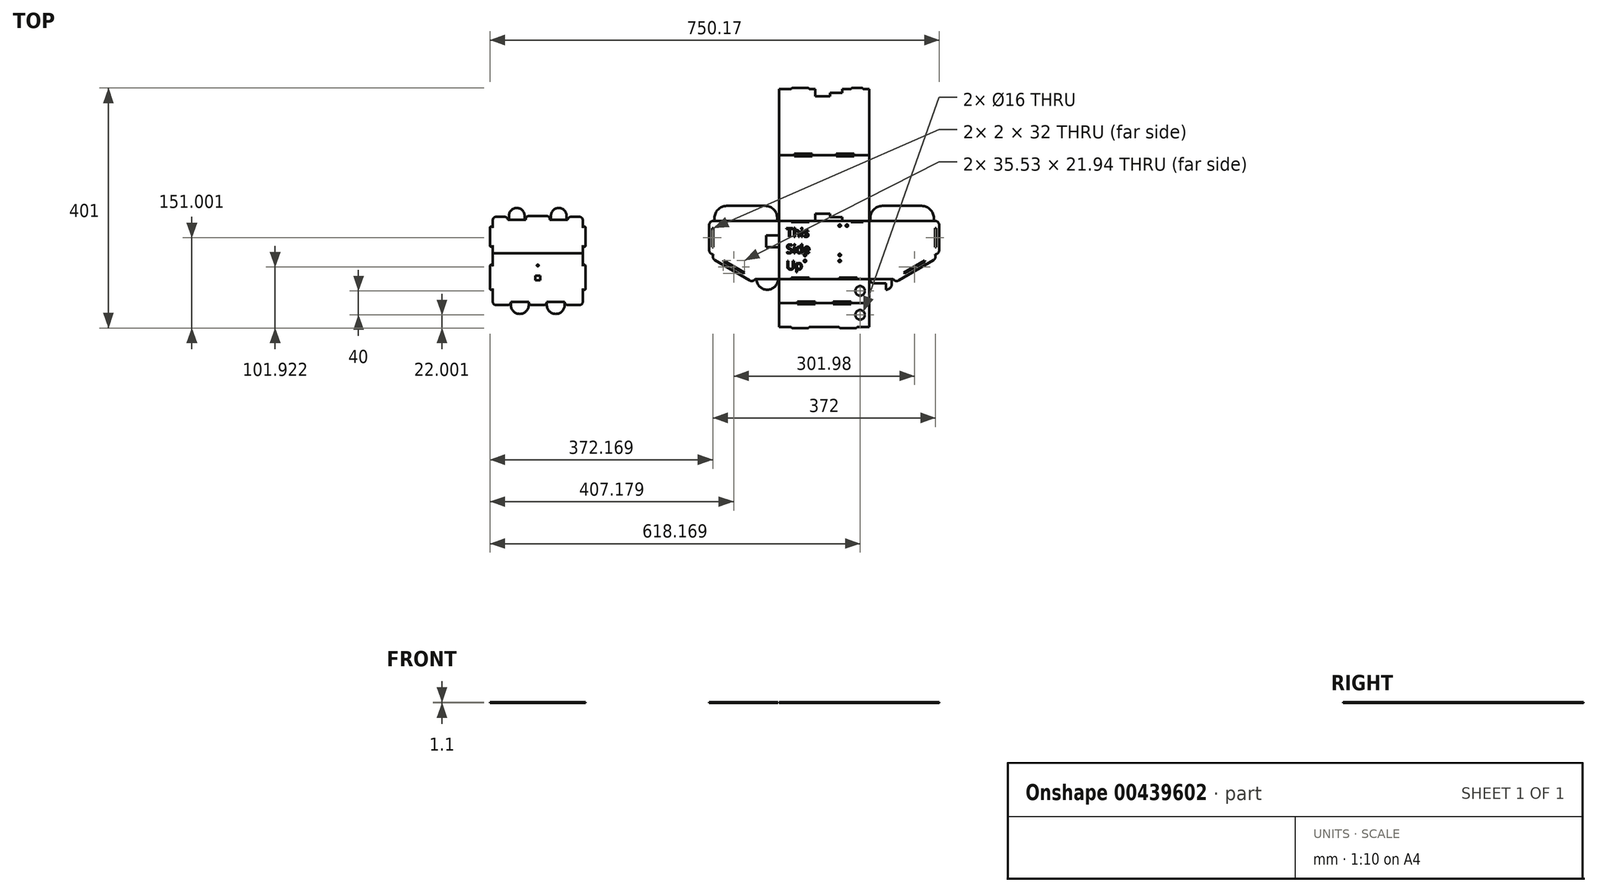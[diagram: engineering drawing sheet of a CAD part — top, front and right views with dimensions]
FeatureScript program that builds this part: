
annotation { "Feature Type Name" : "Feature", "Feature Type Description" : "" }
export const myFeature = defineFeature(function(context is Context, id is Id, definition is map)
    precondition{}
    {
        {
            var Q0;
            Q0=qCreatedBy(makeId("Top.planeOp"),FACE);
            var sketch = newSketch(context, id + "F0", { "sketchPlane" : qUnion([Q0])});
            skLineSegment(sketch, "E0.bottom", {"start": v(-62.15, 54.37) * mm, "end": v(87.85, 54.37) * mm});
            skLineSegment(sketch, "E0.top", {"start": v(-62.15, -42.63) * mm, "end": v(87.85, -42.63) * mm});
            skLineSegment(sketch, "E0.left", {"start": v(-62.15, 54.37) * mm, "end": v(-62.15, -42.63) * mm});
            skLineSegment(sketch, "E0.right", {"start": v(87.85, 54.37) * mm, "end": v(87.85, -42.63) * mm});
            skSolve(sketch);
        }
        {
            var Q0;
            Q0 = qSketchRegion(id + "F0", true);
            extrude(context, id + "F1", {"entities" : qUnion([Q0]), "depth" : 1 * mm});
        }
        {
            var Q0;
            Q0=qCreatedBy(makeId("Top.planeOp"),FACE);
            var sketch = newSketch(context, id + "F2", { "sketchPlane" : qUnion([Q0])});
            skLineSegment(sketch, "E1", {"start": v(-62.15, 54.37) * mm, "end": v(-62.15, -42.63) * mm});
            skLineSegment(sketch, "E2", {"start": v(-172.15, -1.63) * mm, "end": v(-172.15, 54.37) * mm});
            skLineSegment(sketch, "E3", {"start": v(-172.15, 54.37) * mm, "end": v(-62.15, 54.37) * mm});
            skPoint(sketch, "E4", {"position": v(-62.15, 5.87) * mm});
            skLineSegment(sketch, "E5", {"start": v(-62.15, -42.63) * mm, "end": v(-102.15, -42.63) * mm});
            skLineSegment(sketch, "E6", {"start": v(-102.15, -42.63) * mm, "end": v(-172.15, -1.63) * mm});
            skLineSegment(sketch, "E7.bottom", {"start": v(-172.15, 54.37) * mm, "end": v(-172.15, 54.37) * mm});
            skLineSegment(sketch, "E7.top", {"start": v(-172.15, -1.63) * mm, "end": v(-172.15, -1.63) * mm});
            skLineSegment(sketch, "E7.left", {"start": v(-172.15, 54.37) * mm, "end": v(-172.15, -1.63) * mm});
            skLineSegment(sketch, "E7.right", {"start": v(-179.15, 47.37) * mm, "end": v(-179.15, 5.37) * mm});
            skPoint(sketch, "E8.visualSharp", {"position": v(-179.15, 54.37) * mm});
            skArc(sketch, "E8.filletArc", {"start": v(-172.15, 54.37) * mm, "mid": v(-177.1, 52.32) * mm, "end": v(-179.15, 47.37) * mm});
            skPoint(sketch, "E9.visualSharp", {"position": v(-179.15, -1.63) * mm});
            skArc(sketch, "E9.filletArc", {"start": v(-179.15, 5.37) * mm, "mid": v(-177.1, 0.42) * mm, "end": v(-172.15, -1.63) * mm});
            skLineSegment(sketch, "E10", {"start": v(-172.15, -1.63) * mm, "end": v(-102.15, -42.63) * mm});
            skLineSegment(sketch, "E11", {"start": v(-102.15, -42.63) * mm, "end": v(-102.15, -42.63) * mm});
            skLineSegment(sketch, "E12", {"start": v(-111.73, -45.13) * mm, "end": v(-169.65, -11.2) * mm});
            skPoint(sketch, "E13.visualSharp", {"position": v(-175.69, -7.67) * mm});
            skArc(sketch, "E13.filletArc", {"start": v(-172.15, -1.63) * mm, "mid": v(-172.88, -6.94) * mm, "end": v(-169.65, -11.2) * mm});
            skPoint(sketch, "E14.visualSharp", {"position": v(-105.69, -48.67) * mm});
            skArc(sketch, "E14.filletArc", {"start": v(-111.73, -45.13) * mm, "mid": v(-106.42, -45.86) * mm, "end": v(-102.15, -42.63) * mm});
            skSolve(sketch);
        }
        {
            var Q0;
            Q0 = qSketchRegion(id + "F2", true);
            extrude(context, id + "F3", {"entities" : qUnion([Q0]), "depth" : 1 * mm});
        }
        {
            var Q0;
            Q0=makeQuery(id+"F3.opExtrude","CAP_FACE",FACE,{"disambiguationData":[OSD([sQuery(id+"F2.wireOp",EDGE,"E1"),sQuery(id+"F2.wireOp",EDGE,"Gzizx2Oh-LAW5-sl6d-gqP5-EabzbZT4bnnK"),sQuery(id+"F2.wireOp",EDGE,"E2"),sQuery(id+"F2.wireOp",EDGE,"E3")])],"isStart":false});
            var sketch = newSketch(context, id + "F4", { "sketchPlane" : qUnion([Q0])});
            skLineSegment(sketch, "E15.bottom", {"start": v(-62.15, 30.37) * mm, "end": v(-84.15, 30.37) * mm});
            skLineSegment(sketch, "E15.top", {"start": v(-62.15, 10.37) * mm, "end": v(-84.15, 10.37) * mm});
            skLineSegment(sketch, "E15.left", {"start": v(-62.15, 30.37) * mm, "end": v(-62.15, 10.37) * mm});
            skLineSegment(sketch, "E15.right", {"start": v(-84.15, 30.37) * mm, "end": v(-84.15, 10.37) * mm});
            skLineSegment(sketch, "E16", {"start": v(-154.9, -11.74) * mm, "end": v(-120.38, -31.95) * mm});
            skLineSegment(sketch, "E17", {"start": v(-154.9, -11.74) * mm, "end": v(-155.9, -13.46) * mm});
            skLineSegment(sketch, "E18", {"start": v(-155.9, -13.46) * mm, "end": v(-121.39, -33.68) * mm});
            skLineSegment(sketch, "E19", {"start": v(-121.39, -33.68) * mm, "end": v(-120.38, -31.95) * mm});
            skLineSegment(sketch, "E20.bottom", {"start": v(-172.15, 42.37) * mm, "end": v(-174.15, 42.37) * mm});
            skLineSegment(sketch, "E20.top", {"start": v(-172.15, 10.37) * mm, "end": v(-174.15, 10.37) * mm});
            skLineSegment(sketch, "E20.left", {"start": v(-172.15, 42.37) * mm, "end": v(-172.15, 10.37) * mm});
            skLineSegment(sketch, "E20.right", {"start": v(-174.15, 42.37) * mm, "end": v(-174.15, 10.37) * mm});
            skSolve(sketch);
        }
        {
            var Q0;
            Q0 = qSketchRegion(id + "F4", true);
            extrude(context, id + "F5", {"entities" : qUnion([Q0]), "operationType" : NewBodyOperationType.REMOVE, "oppositeDirection" : true, "depth" : 1 * mm});
        }
        {
            var Q0;
            Q0=qCreatedBy(makeId("Top.planeOp"),FACE);
            var sketch = newSketch(context, id + "F6", { "sketchPlane" : qUnion([Q0])});
            skLineSegment(sketch, "E21", {"start": v(87.85, 54.37) * mm, "end": v(197.85, 54.37) * mm});
            skLineSegment(sketch, "E22", {"start": v(197.85, 54.37) * mm, "end": v(197.85, -1.63) * mm});
            skLineSegment(sketch, "E23", {"start": v(87.85, -42.63) * mm, "end": v(87.85, 54.37) * mm});
            skLineSegment(sketch, "E24", {"start": v(87.85, -42.63) * mm, "end": v(127.85, -42.63) * mm});
            skLineSegment(sketch, "E25", {"start": v(127.85, -42.63) * mm, "end": v(197.85, -1.63) * mm});
            skLineSegment(sketch, "E26.bottom", {"start": v(197.85, 54.37) * mm, "end": v(197.85, 54.37) * mm});
            skLineSegment(sketch, "E26.top", {"start": v(197.85, -1.63) * mm, "end": v(197.85, -1.63) * mm});
            skLineSegment(sketch, "E26.right", {"start": v(204.85, 47.37) * mm, "end": v(204.85, 5.37) * mm});
            skLineSegment(sketch, "E27", {"start": v(195.35, -11.2) * mm, "end": v(137.43, -45.13) * mm});
            skLineSegment(sketch, "E28", {"start": v(127.85, -42.63) * mm, "end": v(127.85, -42.63) * mm});
            skPoint(sketch, "E29.visualSharp", {"position": v(131.39, -48.67) * mm});
            skArc(sketch, "E29.filletArc", {"start": v(127.85, -42.63) * mm, "mid": v(132.12, -45.86) * mm, "end": v(137.43, -45.13) * mm});
            skPoint(sketch, "E30.visualSharp", {"position": v(201.39, -7.67) * mm});
            skArc(sketch, "E30.filletArc", {"start": v(195.35, -11.2) * mm, "mid": v(198.58, -6.94) * mm, "end": v(197.85, -1.63) * mm});
            skPoint(sketch, "E31.visualSharp", {"position": v(204.85, -1.63) * mm});
            skArc(sketch, "E31.filletArc", {"start": v(197.85, -1.63) * mm, "mid": v(202.8, 0.42) * mm, "end": v(204.85, 5.37) * mm});
            skPoint(sketch, "E32.visualSharp", {"position": v(204.85, 54.37) * mm});
            skArc(sketch, "E32.filletArc", {"start": v(204.85, 47.37) * mm, "mid": v(202.8, 52.32) * mm, "end": v(197.85, 54.37) * mm});
            skSolve(sketch);
        }
        {
            var Q0;
            Q0 = qSketchRegion(id + "F6", true);
            extrude(context, id + "F7", {"entities" : qUnion([Q0]), "depth" : 1 * mm});
        }
        {
            var Q0;
            Q0=qCreatedBy(makeId("Top.planeOp"),FACE);
            var sketch = newSketch(context, id + "F8", { "sketchPlane" : qUnion([Q0])});
            skLineSegment(sketch, "E33.bottom", {"start": v(-62.15, 54.37) * mm, "end": v(87.85, 54.37) * mm});
            skLineSegment(sketch, "E33.top", {"start": v(-62.15, 164.37) * mm, "end": v(87.85, 164.37) * mm});
            skLineSegment(sketch, "E33.left", {"start": v(-62.15, 54.37) * mm, "end": v(-62.15, 164.37) * mm});
            skLineSegment(sketch, "E33.right", {"start": v(87.85, 54.37) * mm, "end": v(87.85, 164.37) * mm});
            skSolve(sketch);
        }
        {
            var Q0;
            Q0 = qSketchRegion(id + "F8", true);
            extrude(context, id + "F9", {"entities" : qUnion([Q0]), "depth" : 1 * mm});
        }
        {
            var Q0;
            Q0=makeQuery(id+"F9.opExtrude","CAP_FACE",FACE,{"disambiguationData":[OSD([sQuery(id+"F8.wireOp",EDGE,"E33.bottom"),sQuery(id+"F8.wireOp",EDGE,"E33.top"),sQuery(id+"F8.wireOp",EDGE,"E33.left"),sQuery(id+"F8.wireOp",EDGE,"E33.right")])],"isStart":false});
            var sketch = newSketch(context, id + "F10", { "sketchPlane" : qUnion([Q0])});
            skPoint(sketch, "E34.oppositeSnap0", {"position": v(-2.15, 54.37) * mm});
            skLineSegment(sketch, "E34.bottom", {"start": v(42.85, 54.37) * mm, "end": v(-2.15, 54.37) * mm});
            skLineSegment(sketch, "E34.top", {"start": v(42.85, 60.37) * mm, "end": v(-2.15, 60.37) * mm});
            skLineSegment(sketch, "E34.left", {"start": v(42.85, 54.37) * mm, "end": v(42.85, 60.37) * mm});
            skLineSegment(sketch, "E34.right", {"start": v(-2.15, 54.37) * mm, "end": v(-2.15, 60.37) * mm});
            skLineSegment(sketch, "E35.bottom", {"start": v(22.85, 60.37) * mm, "end": v(-2.15, 60.37) * mm});
            skLineSegment(sketch, "E35.top", {"start": v(22.85, 66.37) * mm, "end": v(-2.15, 66.37) * mm});
            skLineSegment(sketch, "E35.left", {"start": v(22.85, 60.37) * mm, "end": v(22.85, 66.37) * mm});
            skLineSegment(sketch, "E35.right", {"start": v(-2.15, 60.37) * mm, "end": v(-2.15, 66.37) * mm});
            skSolve(sketch);
        }
        {
            var Q0;
            Q0 = qSketchRegion(id + "F10", true);
            extrude(context, id + "F11", {"entities" : qUnion([Q0]), "operationType" : NewBodyOperationType.REMOVE, "oppositeDirection" : true, "depth" : 1 * mm});
        }
        {
            var Q0;
            Q0=qCreatedBy(makeId("Top.planeOp"),FACE);
            var sketch = newSketch(context, id + "F12", { "sketchPlane" : qUnion([Q0])});
            skLineSegment(sketch, "E36.bottom", {"start": v(-62.15, 164.37) * mm, "end": v(87.85, 164.37) * mm});
            skLineSegment(sketch, "E36.top", {"start": v(-62.15, 274.37) * mm, "end": v(87.85, 274.37) * mm});
            skLineSegment(sketch, "E36.left", {"start": v(-62.15, 164.37) * mm, "end": v(-62.15, 274.37) * mm});
            skLineSegment(sketch, "E36.right", {"start": v(87.85, 164.37) * mm, "end": v(87.85, 274.37) * mm});
            skLineSegment(sketch, "E37.bottom", {"start": v(-42.15, 274.37) * mm, "end": v(-12.15, 274.37) * mm});
            skLineSegment(sketch, "E37.top", {"start": v(-40.15, 276.37) * mm, "end": v(-14.15, 276.37) * mm});
            skLineSegment(sketch, "E37.left", {"start": v(-42.15, 274.37) * mm, "end": v(-42.15, 274.37) * mm});
            skLineSegment(sketch, "E37.right", {"start": v(-12.15, 274.37) * mm, "end": v(-12.15, 274.37) * mm});
            skLineSegment(sketch, "E38.bottom", {"start": v(57.85, 274.37) * mm, "end": v(77.85, 274.37) * mm});
            skLineSegment(sketch, "E38.top", {"start": v(59.85, 276.37) * mm, "end": v(75.85, 276.37) * mm});
            skLineSegment(sketch, "E38.left", {"start": v(57.85, 274.37) * mm, "end": v(57.85, 274.37) * mm});
            skLineSegment(sketch, "E38.right", {"start": v(77.85, 274.37) * mm, "end": v(77.85, 274.37) * mm});
            skPoint(sketch, "E39.visualSharp", {"position": v(-42.15, 276.37) * mm});
            skArc(sketch, "E39.filletArc", {"start": v(-40.15, 276.37) * mm, "mid": v(-41.57, 275.79) * mm, "end": v(-42.15, 274.37) * mm});
            skPoint(sketch, "E40.visualSharp", {"position": v(-12.15, 276.37) * mm});
            skArc(sketch, "E40.filletArc", {"start": v(-12.15, 274.37) * mm, "mid": v(-12.74, 275.79) * mm, "end": v(-14.15, 276.37) * mm});
            skPoint(sketch, "E41.visualSharp", {"position": v(57.85, 276.37) * mm});
            skArc(sketch, "E41.filletArc", {"start": v(59.85, 276.37) * mm, "mid": v(58.43, 275.79) * mm, "end": v(57.85, 274.37) * mm});
            skPoint(sketch, "E42.visualSharp", {"position": v(77.85, 276.37) * mm});
            skArc(sketch, "E42.filletArc", {"start": v(77.85, 274.37) * mm, "mid": v(77.26, 275.79) * mm, "end": v(75.85, 276.37) * mm});
            skSolve(sketch);
        }
        {
            var Q0;
            Q0 = qSketchRegion(id + "F12", true);
            extrude(context, id + "F13", {"entities" : qUnion([Q0]), "depth" : 1 * mm});
        }
        {
            var Q0;
            Q0=qCreatedBy(makeId("Top.planeOp"),FACE);
            var sketch = newSketch(context, id + "F14", { "sketchPlane" : qUnion([Q0])});
            skLineSegment(sketch, "E43.bottom", {"start": v(-62.15, -42.63) * mm, "end": v(87.85, -42.63) * mm});
            skLineSegment(sketch, "E43.top", {"start": v(-62.15, -82.63) * mm, "end": v(87.85, -82.63) * mm});
            skLineSegment(sketch, "E43.left", {"start": v(-62.15, -42.63) * mm, "end": v(-62.15, -82.63) * mm});
            skLineSegment(sketch, "E43.right", {"start": v(87.85, -42.63) * mm, "end": v(87.85, -82.63) * mm});
            skSolve(sketch);
        }
        {
            var Q0;
            Q0 = qSketchRegion(id + "F14", true);
            extrude(context, id + "F15", {"entities" : qUnion([Q0]), "depth" : 1 * mm});
        }
        {
            var Q0;
            Q0=qCreatedBy(makeId("Top.planeOp"),FACE);
            var sketch = newSketch(context, id + "F16", { "sketchPlane" : qUnion([Q0])});
            skLineSegment(sketch, "E44.bottom", {"start": v(-62.15, -82.63) * mm, "end": v(87.85, -82.63) * mm});
            skLineSegment(sketch, "E44.top", {"start": v(-62.15, -122.63) * mm, "end": v(87.85, -122.63) * mm});
            skLineSegment(sketch, "E44.left", {"start": v(-62.15, -82.63) * mm, "end": v(-62.15, -122.63) * mm});
            skLineSegment(sketch, "E44.right", {"start": v(87.85, -82.63) * mm, "end": v(87.85, -122.63) * mm});
            skLineSegment(sketch, "E45.bottom", {"start": v(-12.15, -122.63) * mm, "end": v(0, -122.63) * mm});
            skLineSegment(sketch, "E45.top", {"start": v(-40.15, -124.63) * mm, "end": v(-14.15, -124.63) * mm});
            skLineSegment(sketch, "E45.left", {"start": v(-42.15, -122.63) * mm, "end": v(-42.15, -122.63) * mm});
            skLineSegment(sketch, "E45.right", {"start": v(-12.15, -122.63) * mm, "end": v(-12.15, -122.63) * mm});
            skLineSegment(sketch, "E46.bottom", {"start": v(37.85, -122.63) * mm, "end": v(67.85, -122.63) * mm});
            skLineSegment(sketch, "E46.top", {"start": v(39.85, -124.63) * mm, "end": v(65.85, -124.63) * mm});
            skLineSegment(sketch, "E46.left", {"start": v(37.85, -122.63) * mm, "end": v(37.85, -122.63) * mm});
            skLineSegment(sketch, "E46.right", {"start": v(67.85, -122.63) * mm, "end": v(67.85, -122.63) * mm});
            skPoint(sketch, "E47.visualSharp", {"position": v(-42.15, -124.63) * mm});
            skArc(sketch, "E47.filletArc", {"start": v(-42.15, -122.63) * mm, "mid": v(-41.57, -124.04) * mm, "end": v(-40.15, -124.63) * mm});
            skPoint(sketch, "E48.visualSharp", {"position": v(-12.15, -124.63) * mm});
            skArc(sketch, "E48.filletArc", {"start": v(-14.15, -124.63) * mm, "mid": v(-12.74, -124.04) * mm, "end": v(-12.15, -122.63) * mm});
            skPoint(sketch, "E49.visualSharp", {"position": v(37.85, -124.63) * mm});
            skArc(sketch, "E49.filletArc", {"start": v(37.85, -122.63) * mm, "mid": v(38.43, -124.04) * mm, "end": v(39.85, -124.63) * mm});
            skPoint(sketch, "E50.visualSharp", {"position": v(67.85, -124.63) * mm});
            skArc(sketch, "E50.filletArc", {"start": v(65.85, -124.63) * mm, "mid": v(67.26, -124.04) * mm, "end": v(67.85, -122.63) * mm});
            skSolve(sketch);
        }
        {
            var Q0;
            Q0 = qSketchRegion(id + "F16", true);
            extrude(context, id + "F17", {"entities" : qUnion([Q0]), "depth" : 1 * mm});
        }
        {
            var Q0;
            Q0 = qSketchRegion(id + "F0", true);
            extrude(context, id + "F18", {"entities" : qUnion([Q0]), "operationType" : NewBodyOperationType.REMOVE, "oppositeDirection" : true, "depth" : 1 * mm});
        }
        {
            var Q0;
            Q0=makeQuery(id+"F1.opExtrude","CAP_FACE",FACE,{"disambiguationData":[OSD([sQuery(id+"F0.wireOp",EDGE,"E0.bottom"),sQuery(id+"F0.wireOp",EDGE,"E0.top"),sQuery(id+"F0.wireOp",EDGE,"E0.left"),sQuery(id+"F0.wireOp",EDGE,"E0.right")])],"isStart":false});
            var sketch = newSketch(context, id + "F19", { "sketchPlane" : qUnion([Q0])});
            skLineSegment(sketch, "E51.bottom", {"start": v(-42.15, -42.63) * mm, "end": v(-12.15, -42.63) * mm});
            skLineSegment(sketch, "E51.top", {"start": v(-42.15, -40.63) * mm, "end": v(-12.15, -40.63) * mm});
            skLineSegment(sketch, "E51.left", {"start": v(-42.15, -42.63) * mm, "end": v(-42.15, -40.63) * mm});
            skLineSegment(sketch, "E51.right", {"start": v(-12.15, -42.63) * mm, "end": v(-12.15, -40.63) * mm});
            skLineSegment(sketch, "E52.bottom", {"start": v(37.85, -42.63) * mm, "end": v(67.85, -42.63) * mm});
            skLineSegment(sketch, "E52.top", {"start": v(37.85, -40.63) * mm, "end": v(67.85, -40.63) * mm});
            skLineSegment(sketch, "E52.left", {"start": v(37.85, -42.63) * mm, "end": v(37.85, -40.63) * mm});
            skLineSegment(sketch, "E52.right", {"start": v(67.85, -42.63) * mm, "end": v(67.85, -40.63) * mm});
            skLineSegment(sketch, "E53.bottom", {"start": v(-42.15, 54.37) * mm, "end": v(-12.15, 54.37) * mm});
            skLineSegment(sketch, "E53.top", {"start": v(-42.15, 52.18) * mm, "end": v(-12.15, 52.18) * mm});
            skLineSegment(sketch, "E53.left", {"start": v(-42.15, 54.37) * mm, "end": v(-42.15, 52.18) * mm});
            skLineSegment(sketch, "E53.right", {"start": v(-12.15, 54.37) * mm, "end": v(-12.15, 52.18) * mm});
            skLineSegment(sketch, "E54.bottom", {"start": v(57.85, 54.37) * mm, "end": v(77.85, 54.37) * mm});
            skLineSegment(sketch, "E54.top", {"start": v(57.85, 52.37) * mm, "end": v(77.85, 52.37) * mm});
            skLineSegment(sketch, "E54.left", {"start": v(57.85, 54.37) * mm, "end": v(57.85, 52.37) * mm});
            skLineSegment(sketch, "E54.right", {"start": v(77.85, 54.37) * mm, "end": v(77.85, 52.37) * mm});
            skCircle(sketch, "E55", {"center": v(50.85, 46.37) * mm, "radius": 2 * mm});
            skCircle(sketch, "E56", {"center": v(38.85, 46.37) * mm, "radius": 2 * mm});
            skCircle(sketch, "E57", {"center": v(38.85, -2.63) * mm, "radius": 2 * mm});
            skCircle(sketch, "E58", {"center": v(38.85, -12.63) * mm, "radius": 2 * mm});
            skCircle(sketch, "E59", {"center": v(-19.15, -12.63) * mm, "radius": 2 * mm});
            skCircle(sketch, "E60", {"center": v(-19.15, -2.63) * mm, "radius": 2 * mm});
            skSolve(sketch);
        }
        {
            var Q0;
            Q0 = qSketchRegion(id + "F19", true);
            extrude(context, id + "F20", {"entities" : qUnion([Q0]), "operationType" : NewBodyOperationType.REMOVE, "oppositeDirection" : true, "depth" : 1 * mm});
        }
        {
            var Q0;
            Q0=makeQuery(id+"F9.opExtrude","CAP_FACE",FACE,{"disambiguationData":[OSD([sQuery(id+"F8.wireOp",EDGE,"E33.bottom"),sQuery(id+"F8.wireOp",EDGE,"E33.top"),sQuery(id+"F8.wireOp",EDGE,"E33.left"),sQuery(id+"F8.wireOp",EDGE,"E33.right")])],"isStart":false});
            var sketch = newSketch(context, id + "F21", { "sketchPlane" : qUnion([Q0])});
            skLineSegment(sketch, "E61.bottom", {"start": v(-37.15, 164.37) * mm, "end": v(-7.15, 164.37) * mm});
            skLineSegment(sketch, "E61.top", {"start": v(-37.15, 162.37) * mm, "end": v(-7.15, 162.37) * mm});
            skLineSegment(sketch, "E61.left", {"start": v(-37.15, 164.37) * mm, "end": v(-37.15, 162.37) * mm});
            skLineSegment(sketch, "E61.right", {"start": v(-7.15, 164.37) * mm, "end": v(-7.15, 162.37) * mm});
            skLineSegment(sketch, "E62.bottom", {"start": v(32.85, 164.37) * mm, "end": v(62.85, 164.37) * mm});
            skLineSegment(sketch, "E62.top", {"start": v(32.85, 162.37) * mm, "end": v(62.85, 162.37) * mm});
            skLineSegment(sketch, "E62.left", {"start": v(32.85, 164.37) * mm, "end": v(32.85, 162.37) * mm});
            skLineSegment(sketch, "E62.right", {"start": v(62.85, 164.37) * mm, "end": v(62.85, 162.37) * mm});
            skSolve(sketch);
        }
        {
            var Q0;
            Q0 = qSketchRegion(id + "F21", true);
            extrude(context, id + "F22", {"entities" : qUnion([Q0]), "operationType" : NewBodyOperationType.REMOVE, "oppositeDirection" : true, "depth" : 2 * mm});
        }
        {
            var Q0;
            Q0=makeQuery(id+"F13.opExtrude","CAP_FACE",FACE,{"disambiguationData":[OSD([sQuery(id+"F12.wireOp",EDGE,"E36.bottom"),sQuery(id+"F12.wireOp",EDGE,"E36.top"),sQuery(id+"F12.wireOp",EDGE,"E36.left"),sQuery(id+"F12.wireOp",EDGE,"E36.right"),sQuery(id+"F12.wireOp",EDGE,"E37.top"),sQuery(id+"F12.wireOp",EDGE,"E37.left"),sQuery(id+"F12.wireOp",EDGE,"E37.right"),sQuery(id+"F12.wireOp",EDGE,"E38.top"),sQuery(id+"F12.wireOp",EDGE,"E38.left"),sQuery(id+"F12.wireOp",EDGE,"E38.right")])],"isStart":false});
            var sketch = newSketch(context, id + "F23", { "sketchPlane" : qUnion([Q0])});
            skLineSegment(sketch, "E63", {"start": v(42.85, 274.37) * mm, "end": v(42.85, 268.37) * mm});
            skLineSegment(sketch, "E64", {"start": v(42.85, 268.37) * mm, "end": v(22.85, 268.37) * mm});
            skLineSegment(sketch, "E65", {"start": v(22.85, 268.37) * mm, "end": v(22.85, 262.37) * mm});
            skLineSegment(sketch, "E66", {"start": v(22.85, 262.37) * mm, "end": v(-2.15, 262.37) * mm});
            skLineSegment(sketch, "E67", {"start": v(-2.15, 262.37) * mm, "end": v(-2.15, 274.37) * mm});
            skLineSegment(sketch, "E68", {"start": v(-2.15, 274.37) * mm, "end": v(42.85, 274.37) * mm});
            skLineSegment(sketch, "E69.bottom", {"start": v(-37.15, 164.37) * mm, "end": v(-7.15, 164.37) * mm});
            skLineSegment(sketch, "E69.top", {"start": v(-37.15, 166.37) * mm, "end": v(-7.15, 166.37) * mm});
            skLineSegment(sketch, "E69.left", {"start": v(-37.15, 164.37) * mm, "end": v(-37.15, 166.37) * mm});
            skLineSegment(sketch, "E69.right", {"start": v(-7.15, 164.37) * mm, "end": v(-7.15, 166.37) * mm});
            skLineSegment(sketch, "E70.bottom", {"start": v(32.85, 164.37) * mm, "end": v(62.85, 164.37) * mm});
            skLineSegment(sketch, "E70.top", {"start": v(32.85, 166.37) * mm, "end": v(62.85, 166.37) * mm});
            skLineSegment(sketch, "E70.left", {"start": v(32.85, 164.37) * mm, "end": v(32.85, 166.37) * mm});
            skLineSegment(sketch, "E70.right", {"start": v(62.85, 164.37) * mm, "end": v(62.85, 166.37) * mm});
            skSolve(sketch);
        }
        {
            var Q0;
            Q0 = qSketchRegion(id + "F23", true);
            extrude(context, id + "F24", {"entities" : qUnion([Q0]), "operationType" : NewBodyOperationType.REMOVE, "oppositeDirection" : true, "depth" : 2 * mm});
        }
        {
            var Q0;
            Q0=qCreatedBy(makeId("Top.planeOp"),FACE);
            var sketch = newSketch(context, id + "F25", { "sketchPlane" : qUnion([Q0])});
            skArc(sketch, "E71", {"start": v(-100.15, -42.63) * mm, "mid": v(-82.15, -60.63) * mm, "end": v(-64.15, -42.63) * mm});
            skLineSegment(sketch, "E72", {"start": v(-100.15, -42.63) * mm, "end": v(-64.15, -42.63) * mm});
            skSolve(sketch);
        }
        {
            var Q0;
            Q0 = qSketchRegion(id + "F25", true);
            extrude(context, id + "F26", {"entities" : qUnion([Q0]), "depth" : 1 * mm});
        }
        {
            var Q0;
            Q0=qCreatedBy(makeId("Top.planeOp"),FACE);
            var sketch = newSketch(context, id + "F27", { "sketchPlane" : qUnion([Q0])});
            skLineSegment(sketch, "E73.bottom", {"start": v(125.85, -42.63) * mm, "end": v(115.85, -42.63) * mm});
            skLineSegment(sketch, "E73.top", {"start": v(115.85, -60.63) * mm, "end": v(115.85, -60.63) * mm});
            skLineSegment(sketch, "E73.left", {"start": v(125.85, -42.63) * mm, "end": v(125.85, -50.63) * mm});
            skLineSegment(sketch, "E73.right", {"start": v(115.85, -42.63) * mm, "end": v(115.85, -60.63) * mm});
            skPoint(sketch, "E74.visualSharp", {"position": v(125.85, -60.63) * mm});
            skArc(sketch, "E74.filletArc", {"start": v(115.85, -60.63) * mm, "mid": v(122.92, -57.7) * mm, "end": v(125.85, -50.63) * mm});
            skLineSegment(sketch, "E75.bottom", {"start": v(89.85, -42.63) * mm, "end": v(125.85, -42.63) * mm});
            skLineSegment(sketch, "E75.top", {"start": v(94.85, -49.63) * mm, "end": v(125.85, -49.63) * mm});
            skLineSegment(sketch, "E75.left", {"start": v(89.85, -42.63) * mm, "end": v(89.85, -44.63) * mm});
            skLineSegment(sketch, "E75.right", {"start": v(125.85, -42.63) * mm, "end": v(125.85, -49.63) * mm});
            skPoint(sketch, "E76.visualSharp", {"position": v(89.85, -49.63) * mm});
            skArc(sketch, "E76.filletArc", {"start": v(89.85, -44.63) * mm, "mid": v(91.31, -48.16) * mm, "end": v(94.85, -49.63) * mm});
            skSolve(sketch);
        }
        {
            var Q0;
            Q0 = qSketchRegion(id + "F27", true);
            extrude(context, id + "F28", {"entities" : qUnion([Q0]), "depth" : 1 * mm});
        }
        {
            var Q0;
            Q0=makeQuery(id+"F17.opExtrude","CAP_FACE",FACE,{"disambiguationData":[OSD([sQuery(id+"F16.wireOp",EDGE,"E44.bottom"),sQuery(id+"F16.wireOp",EDGE,"E44.top"),sQuery(id+"F16.wireOp",EDGE,"E44.left"),sQuery(id+"F16.wireOp",EDGE,"E44.right"),sQuery(id+"F16.wireOp",EDGE,"E45.bottom"),sQuery(id+"F16.wireOp",EDGE,"E45.top"),sQuery(id+"F16.wireOp",EDGE,"E45.left"),sQuery(id+"F16.wireOp",EDGE,"E45.right"),sQuery(id+"F16.wireOp",EDGE,"E46.top"),sQuery(id+"F16.wireOp",EDGE,"E46.left"),sQuery(id+"F16.wireOp",EDGE,"E46.right")])],"isStart":false});
            var sketch = newSketch(context, id + "F29", { "sketchPlane" : qUnion([Q0])});
            skLineSegment(sketch, "E77.bottom", {"start": v(-32.15, -82.63) * mm, "end": v(-2.15, -82.63) * mm});
            skLineSegment(sketch, "E77.top", {"start": v(-32.15, -84.63) * mm, "end": v(-2.15, -84.63) * mm});
            skLineSegment(sketch, "E77.left", {"start": v(-32.15, -82.63) * mm, "end": v(-32.15, -84.63) * mm});
            skLineSegment(sketch, "E77.right", {"start": v(-2.15, -82.63) * mm, "end": v(-2.15, -84.63) * mm});
            skLineSegment(sketch, "E78.bottom", {"start": v(27.85, -82.63) * mm, "end": v(57.85, -82.63) * mm});
            skLineSegment(sketch, "E78.top", {"start": v(27.85, -84.63) * mm, "end": v(57.85, -84.63) * mm});
            skLineSegment(sketch, "E78.left", {"start": v(27.85, -82.63) * mm, "end": v(27.85, -84.63) * mm});
            skLineSegment(sketch, "E78.right", {"start": v(57.85, -82.63) * mm, "end": v(57.85, -84.63) * mm});
            skCircle(sketch, "E79", {"center": v(72.85, -102.63) * mm, "radius": 8 * mm});
            skSolve(sketch);
        }
        {
            var Q0;
            Q0 = qSketchRegion(id + "F29", true);
            extrude(context, id + "F30", {"entities" : qUnion([Q0]), "operationType" : NewBodyOperationType.REMOVE, "oppositeDirection" : true, "depth" : 1 * mm});
        }
        {
            var Q0;
            Q0=makeQuery(id+"F15.opExtrude","CAP_FACE",FACE,{"disambiguationData":[OSD([sQuery(id+"F14.wireOp",EDGE,"E43.bottom"),sQuery(id+"F14.wireOp",EDGE,"E43.top"),sQuery(id+"F14.wireOp",EDGE,"E43.left"),sQuery(id+"F14.wireOp",EDGE,"E43.right")])],"isStart":false});
            var sketch = newSketch(context, id + "F31", { "sketchPlane" : qUnion([Q0])});
            skLineSegment(sketch, "E80.bottom", {"start": v(-32.15, -82.63) * mm, "end": v(-2.15, -82.63) * mm});
            skLineSegment(sketch, "E80.top", {"start": v(-32.15, -80.63) * mm, "end": v(-2.15, -80.63) * mm});
            skLineSegment(sketch, "E80.left", {"start": v(-32.15, -82.63) * mm, "end": v(-32.15, -80.63) * mm});
            skLineSegment(sketch, "E80.right", {"start": v(-2.15, -82.63) * mm, "end": v(-2.15, -80.63) * mm});
            skLineSegment(sketch, "E81.bottom", {"start": v(27.85, -82.63) * mm, "end": v(57.85, -82.63) * mm});
            skLineSegment(sketch, "E81.top", {"start": v(27.85, -80.63) * mm, "end": v(57.85, -80.63) * mm});
            skLineSegment(sketch, "E81.left", {"start": v(27.85, -82.63) * mm, "end": v(27.85, -80.63) * mm});
            skLineSegment(sketch, "E81.right", {"start": v(57.85, -82.63) * mm, "end": v(57.85, -80.63) * mm});
            skCircle(sketch, "E82", {"center": v(72.85, -62.63) * mm, "radius": 8 * mm});
            skSolve(sketch);
        }
        {
            var Q0;
            Q0 = qSketchRegion(id + "F31", true);
            extrude(context, id + "F32", {"entities" : qUnion([Q0]), "operationType" : NewBodyOperationType.REMOVE, "oppositeDirection" : true, "depth" : 1 * mm});
        }
        {
            var Q0;
            Q0=qCreatedBy(makeId("Top.planeOp"),FACE);
            var sketch = newSketch(context, id + "F33", { "sketchPlane" : qUnion([Q0])});
            skLineSegment(sketch, "E83", {"start": v(-170.15, 54.37) * mm, "end": v(-64.15, 54.37) * mm});
            skLineSegment(sketch, "E84.bottom", {"start": v(-170.15, 54.37) * mm, "end": v(-65.48, 54.37) * mm});
            skLineSegment(sketch, "E84.top", {"start": v(-150.15, 79.37) * mm, "end": v(-85.48, 79.37) * mm});
            skLineSegment(sketch, "E84.left", {"start": v(-170.15, 54.37) * mm, "end": v(-170.15, 59.37) * mm});
            skLineSegment(sketch, "E84.right", {"start": v(-65.48, 54.37) * mm, "end": v(-65.48, 59.37) * mm});
            skPoint(sketch, "E85.visualSharp", {"position": v(-170.15, 79.37) * mm});
            skArc(sketch, "E85.filletArc", {"start": v(-150.15, 79.37) * mm, "mid": v(-164.3, 73.51) * mm, "end": v(-170.15, 59.37) * mm});
            skPoint(sketch, "E86.visualSharp", {"position": v(-65.48, 79.37) * mm});
            skArc(sketch, "E86.filletArc", {"start": v(-65.48, 59.37) * mm, "mid": v(-71.34, 73.51) * mm, "end": v(-85.48, 79.37) * mm});
            skSolve(sketch);
        }
        {
            var Q0;
            Q0 = qSketchRegion(id + "F33", true);
            extrude(context, id + "F34", {"entities" : qUnion([Q0]), "depth" : 1 * mm});
        }
        {
            var Q0;
            Q0=qCreatedBy(makeId("Top.planeOp"),FACE);
            var sketch = newSketch(context, id + "F35", { "sketchPlane" : qUnion([Q0])});
            skLineSegment(sketch, "E87", {"start": v(89.85, 54.37) * mm, "end": v(195.85, 54.37) * mm});
            skLineSegment(sketch, "E88.top", {"start": v(109.85, 79.37) * mm, "end": v(175.85, 79.37) * mm});
            skLineSegment(sketch, "E88.left", {"start": v(89.85, 54.37) * mm, "end": v(89.85, 59.37) * mm});
            skLineSegment(sketch, "E88.right", {"start": v(195.85, 54.37) * mm, "end": v(195.85, 59.37) * mm});
            skPoint(sketch, "E89.visualSharp", {"position": v(89.85, 79.37) * mm});
            skArc(sketch, "E89.filletArc", {"start": v(109.85, 79.37) * mm, "mid": v(95.7, 73.51) * mm, "end": v(89.85, 59.37) * mm});
            skPoint(sketch, "E90.visualSharp", {"position": v(195.85, 79.37) * mm});
            skArc(sketch, "E90.filletArc", {"start": v(195.85, 59.37) * mm, "mid": v(190, 73.51) * mm, "end": v(175.85, 79.37) * mm});
            skSolve(sketch);
        }
        {
            var Q0;
            Q0 = qSketchRegion(id + "F35", true);
            extrude(context, id + "F36", {"entities" : qUnion([Q0]), "depth" : 1 * mm});
        }
        {
            var Q0;
            Q0=qCreatedBy(makeId("Top.planeOp"),FACE);
            var sketch = newSketch(context, id + "F37", { "sketchPlane" : qUnion([Q0])});
            skLineSegment(sketch, "E91.bottom", {"start": v(-540.32, 56) * mm, "end": v(-390.32, 56) * mm});
            skLineSegment(sketch, "E91.top", {"start": v(-540.32, 0) * mm, "end": v(-390.32, 0) * mm});
            skLineSegment(sketch, "E91.left", {"start": v(-540.32, 56) * mm, "end": v(-540.32, 0) * mm});
            skLineSegment(sketch, "E91.right", {"start": v(-390.32, 56) * mm, "end": v(-390.32, 0) * mm});
            skLineSegment(sketch, "E92.bottom", {"start": v(-540.32, 56) * mm, "end": v(-515.32, 56) * mm});
            skLineSegment(sketch, "E92.top", {"start": v(-535.32, 61) * mm, "end": v(-520.32, 61) * mm});
            skLineSegment(sketch, "E92.left", {"start": v(-540.32, 56) * mm, "end": v(-540.32, 56) * mm});
            skLineSegment(sketch, "E92.right", {"start": v(-515.32, 56) * mm, "end": v(-515.32, 56) * mm});
            skLineSegment(sketch, "E93.bottom", {"start": v(-415.32, 56) * mm, "end": v(-390.32, 56) * mm});
            skLineSegment(sketch, "E93.top", {"start": v(-410.32, 61) * mm, "end": v(-395.32, 61) * mm});
            skLineSegment(sketch, "E93.left", {"start": v(-415.32, 56) * mm, "end": v(-415.32, 56) * mm});
            skLineSegment(sketch, "E93.right", {"start": v(-390.32, 56) * mm, "end": v(-390.32, 56) * mm});
            skPoint(sketch, "E94.visualSharp", {"position": v(-415.32, 61) * mm});
            skArc(sketch, "E94.filletArc", {"start": v(-410.32, 61) * mm, "mid": v(-413.85, 59.54) * mm, "end": v(-415.32, 56) * mm});
            skPoint(sketch, "E95.visualSharp", {"position": v(-390.32, 61) * mm});
            skArc(sketch, "E95.filletArc", {"start": v(-390.32, 56) * mm, "mid": v(-391.78, 59.54) * mm, "end": v(-395.32, 61) * mm});
            skPoint(sketch, "E96.visualSharp", {"position": v(-515.32, 61) * mm});
            skArc(sketch, "E96.filletArc", {"start": v(-515.32, 56) * mm, "mid": v(-516.78, 59.54) * mm, "end": v(-520.32, 61) * mm});
            skPoint(sketch, "E97.visualSharp", {"position": v(-540.32, 61) * mm});
            skArc(sketch, "E97.filletArc", {"start": v(-535.32, 61) * mm, "mid": v(-538.85, 59.54) * mm, "end": v(-540.32, 56) * mm});
            skLineSegment(sketch, "E98.bottom", {"start": v(-485.32, 56) * mm, "end": v(-445.32, 56) * mm});
            skLineSegment(sketch, "E98.top", {"start": v(-480.32, 62.41) * mm, "end": v(-450.32, 62.41) * mm});
            skLineSegment(sketch, "E98.left", {"start": v(-485.32, 56) * mm, "end": v(-485.32, 57.41) * mm});
            skLineSegment(sketch, "E98.right", {"start": v(-445.32, 56) * mm, "end": v(-445.32, 57.41) * mm});
            skPoint(sketch, "E99.visualSharp", {"position": v(-485.32, 62.41) * mm});
            skArc(sketch, "E99.filletArc", {"start": v(-480.32, 62.41) * mm, "mid": v(-483.85, 60.95) * mm, "end": v(-485.32, 57.41) * mm});
            skPoint(sketch, "E100.visualSharp", {"position": v(-445.32, 62.41) * mm});
            skArc(sketch, "E100.filletArc", {"start": v(-445.32, 57.41) * mm, "mid": v(-446.78, 60.95) * mm, "end": v(-450.32, 62.41) * mm});
            skLineSegment(sketch, "E101.bottom", {"start": v(-540.32, 45) * mm, "end": v(-540.32, 45) * mm});
            skLineSegment(sketch, "E101.top", {"start": v(-540.32, 12) * mm, "end": v(-540.32, 12) * mm});
            skPoint(sketch, "E102.visualSharp", {"position": v(-545.32, 45) * mm});
            skLineSegment(sketch, "E103.bottom", {"start": v(-542.82, 45) * mm, "end": v(-542.82, 45) * mm});
            skLineSegment(sketch, "E103.top", {"start": v(-542.82, 11) * mm, "end": v(-542.82, 11) * mm});
            skLineSegment(sketch, "E103.left", {"start": v(-540.32, 42.5) * mm, "end": v(-540.32, 13.5) * mm});
            skLineSegment(sketch, "E103.right", {"start": v(-545.32, 42.5) * mm, "end": v(-545.32, 13.5) * mm});
            skArc(sketch, "E104.filletArc", {"start": v(-542.82, 45) * mm, "mid": v(-544.58, 44.27) * mm, "end": v(-545.32, 42.5) * mm});
            skPoint(sketch, "E105.visualSharp", {"position": v(-540.32, 45) * mm});
            skArc(sketch, "E105.filletArc", {"start": v(-540.32, 42.5) * mm, "mid": v(-541.05, 44.27) * mm, "end": v(-542.82, 45) * mm});
            skPoint(sketch, "E106.visualSharp", {"position": v(-545.32, 11) * mm});
            skArc(sketch, "E106.filletArc", {"start": v(-545.32, 13.5) * mm, "mid": v(-544.58, 11.73) * mm, "end": v(-542.82, 11) * mm});
            skPoint(sketch, "E107.visualSharp", {"position": v(-540.32, 11) * mm});
            skArc(sketch, "E107.filletArc", {"start": v(-542.82, 11) * mm, "mid": v(-541.05, 11.73) * mm, "end": v(-540.32, 13.5) * mm});
            skLineSegment(sketch, "E108.bottom", {"start": v(-387.82, 45) * mm, "end": v(-387.82, 45) * mm});
            skLineSegment(sketch, "E108.top", {"start": v(-387.82, 11) * mm, "end": v(-387.82, 11) * mm});
            skLineSegment(sketch, "E108.left", {"start": v(-390.32, 42.5) * mm, "end": v(-390.32, 13.5) * mm});
            skLineSegment(sketch, "E108.right", {"start": v(-385.32, 42.5) * mm, "end": v(-385.32, 13.5) * mm});
            skArc(sketch, "E109.filletArc", {"start": v(-385.32, 42.5) * mm, "mid": v(-386.05, 44.27) * mm, "end": v(-387.82, 45) * mm});
            skPoint(sketch, "E110.visualSharp", {"position": v(-385.32, 11) * mm});
            skArc(sketch, "E110.filletArc", {"start": v(-387.82, 11) * mm, "mid": v(-386.05, 11.73) * mm, "end": v(-385.32, 13.5) * mm});
            skPoint(sketch, "E111.visualSharp", {"position": v(-390.32, 11) * mm});
            skArc(sketch, "E111.filletArc", {"start": v(-390.32, 13.5) * mm, "mid": v(-389.58, 11.73) * mm, "end": v(-387.82, 11) * mm});
            skPoint(sketch, "E112.visualSharp", {"position": v(-390.32, 45) * mm});
            skArc(sketch, "E112.filletArc", {"start": v(-387.82, 45) * mm, "mid": v(-389.58, 44.27) * mm, "end": v(-390.32, 42.5) * mm});
            skSolve(sketch);
        }
        {
            var Q0;
            Q0 = qSketchRegion(id + "F37", true);
            extrude(context, id + "F38", {"entities" : qUnion([Q0]), "depth" : 1 * mm});
        }
        {
            var Q0;
            Q0=qCreatedBy(makeId("Top.planeOp"),FACE);
            var sketch = newSketch(context, id + "F39", { "sketchPlane" : qUnion([Q0])});
            skLineSegment(sketch, "E113.bottom", {"start": v(-513.32, 56) * mm, "end": v(-487.32, 56) * mm});
            skLineSegment(sketch, "E113.top", {"start": v(-500.32, 76) * mm, "end": v(-500.32, 76) * mm});
            skLineSegment(sketch, "E113.left", {"start": v(-513.32, 56) * mm, "end": v(-513.32, 63) * mm});
            skLineSegment(sketch, "E113.right", {"start": v(-487.32, 56) * mm, "end": v(-487.32, 63) * mm});
            skLineSegment(sketch, "E114.bottom", {"start": v(-443.32, 56) * mm, "end": v(-417.32, 56) * mm});
            skLineSegment(sketch, "E114.top", {"start": v(-430.32, 76) * mm, "end": v(-430.32, 76) * mm});
            skLineSegment(sketch, "E114.left", {"start": v(-443.32, 56) * mm, "end": v(-443.32, 63) * mm});
            skLineSegment(sketch, "E114.right", {"start": v(-417.32, 56) * mm, "end": v(-417.32, 63) * mm});
            skPoint(sketch, "E115.visualSharp", {"position": v(-513.32, 76) * mm});
            skArc(sketch, "E115.filletArc", {"start": v(-500.32, 76) * mm, "mid": v(-509.5, 72.2) * mm, "end": v(-513.32, 63) * mm});
            skPoint(sketch, "E116.visualSharp", {"position": v(-487.32, 76) * mm});
            skArc(sketch, "E116.filletArc", {"start": v(-487.32, 63) * mm, "mid": v(-491.12, 72.2) * mm, "end": v(-500.32, 76) * mm});
            skPoint(sketch, "E117.visualSharp", {"position": v(-443.32, 76) * mm});
            skArc(sketch, "E117.filletArc", {"start": v(-430.32, 76) * mm, "mid": v(-439.5, 72.2) * mm, "end": v(-443.32, 63) * mm});
            skPoint(sketch, "E118.visualSharp", {"position": v(-417.32, 76) * mm});
            skArc(sketch, "E118.filletArc", {"start": v(-417.32, 63) * mm, "mid": v(-421.12, 72.2) * mm, "end": v(-430.32, 76) * mm});
            skSolve(sketch);
        }
        {
            var Q0;
            Q0 = qSketchRegion(id + "F39", true);
            extrude(context, id + "F40", {"entities" : qUnion([Q0]), "depth" : 1 * mm});
        }
        {
            var Q0;
            Q0=qCreatedBy(makeId("Top.planeOp"),FACE);
            var sketch = newSketch(context, id + "F41", { "sketchPlane" : qUnion([Q0])});
            skLineSegment(sketch, "E119.bottom", {"start": v(-540.32, 0) * mm, "end": v(-390.32, 0) * mm});
            skLineSegment(sketch, "E119.top", {"start": v(-540.32, -81.12) * mm, "end": v(-390.32, -81.12) * mm});
            skLineSegment(sketch, "E119.left", {"start": v(-540.32, 0) * mm, "end": v(-540.32, -81.12) * mm});
            skLineSegment(sketch, "E119.right", {"start": v(-390.32, 0) * mm, "end": v(-390.32, -81.12) * mm});
            skLineSegment(sketch, "E120.bottom", {"start": v(-540.32, -81.12) * mm, "end": v(-510.32, -81.12) * mm});
            skLineSegment(sketch, "E120.top", {"start": v(-535.32, -86.12) * mm, "end": v(-515.32, -86.12) * mm});
            skLineSegment(sketch, "E120.left", {"start": v(-540.32, -81.12) * mm, "end": v(-540.32, -81.12) * mm});
            skLineSegment(sketch, "E120.right", {"start": v(-510.32, -81.12) * mm, "end": v(-510.32, -81.12) * mm});
            skLineSegment(sketch, "E121.bottom", {"start": v(-480.32, -81.12) * mm, "end": v(-450.32, -81.12) * mm});
            skLineSegment(sketch, "E121.top", {"start": v(-475.32, -86.12) * mm, "end": v(-455.32, -86.12) * mm});
            skLineSegment(sketch, "E121.left", {"start": v(-480.32, -81.12) * mm, "end": v(-480.32, -81.12) * mm});
            skLineSegment(sketch, "E121.right", {"start": v(-450.32, -81.12) * mm, "end": v(-450.32, -81.12) * mm});
            skLineSegment(sketch, "E122.bottom", {"start": v(-420.32, -81.12) * mm, "end": v(-390.32, -81.12) * mm});
            skLineSegment(sketch, "E122.top", {"start": v(-415.32, -86.12) * mm, "end": v(-395.32, -86.12) * mm});
            skLineSegment(sketch, "E122.left", {"start": v(-420.32, -81.12) * mm, "end": v(-420.32, -81.12) * mm});
            skLineSegment(sketch, "E122.right", {"start": v(-390.32, -81.12) * mm, "end": v(-390.32, -81.12) * mm});
            skPoint(sketch, "E123.visualSharp", {"position": v(-540.32, -86.12) * mm});
            skArc(sketch, "E123.filletArc", {"start": v(-540.32, -81.12) * mm, "mid": v(-538.85, -84.66) * mm, "end": v(-535.32, -86.12) * mm});
            skPoint(sketch, "E124.visualSharp", {"position": v(-510.32, -86.12) * mm});
            skArc(sketch, "E124.filletArc", {"start": v(-515.32, -86.12) * mm, "mid": v(-511.78, -84.66) * mm, "end": v(-510.32, -81.12) * mm});
            skPoint(sketch, "E125.visualSharp", {"position": v(-480.32, -86.12) * mm});
            skArc(sketch, "E125.filletArc", {"start": v(-480.32, -81.12) * mm, "mid": v(-478.85, -84.66) * mm, "end": v(-475.32, -86.12) * mm});
            skPoint(sketch, "E126.visualSharp", {"position": v(-450.32, -86.12) * mm});
            skArc(sketch, "E126.filletArc", {"start": v(-455.32, -86.12) * mm, "mid": v(-451.78, -84.66) * mm, "end": v(-450.32, -81.12) * mm});
            skPoint(sketch, "E127.visualSharp", {"position": v(-420.32, -86.12) * mm});
            skArc(sketch, "E127.filletArc", {"start": v(-420.32, -81.12) * mm, "mid": v(-418.85, -84.66) * mm, "end": v(-415.32, -86.12) * mm});
            skPoint(sketch, "E128.visualSharp", {"position": v(-390.32, -86.12) * mm});
            skArc(sketch, "E128.filletArc", {"start": v(-395.32, -86.12) * mm, "mid": v(-391.78, -84.66) * mm, "end": v(-390.32, -81.12) * mm});
            skCircle(sketch, "E129", {"center": v(-465.21, -20) * mm, "radius": 1.5 * mm});
            skCircle(sketch, "E130", {"center": v(-351.7, -41.12) * mm, "radius": 1 * mm});
            skLineSegment(sketch, "E131.left", {"start": v(-390.32, -20) * mm, "end": v(-390.32, -60) * mm});
            skLineSegment(sketch, "E132.bottom", {"start": v(-469.32, -45.12) * mm, "end": v(-461.32, -45.12) * mm});
            skLineSegment(sketch, "E132.top", {"start": v(-469.32, -37.12) * mm, "end": v(-461.32, -37.12) * mm});
            skLineSegment(sketch, "E132.left", {"start": v(-469.32, -45.12) * mm, "end": v(-469.32, -37.12) * mm});
            skLineSegment(sketch, "E132.right", {"start": v(-461.32, -45.12) * mm, "end": v(-461.32, -37.12) * mm});
            skLineSegment(sketch, "E133.bottom", {"start": v(-542.82, -19) * mm, "end": v(-542.82, -19) * mm});
            skLineSegment(sketch, "E133.top", {"start": v(-542.82, -61) * mm, "end": v(-542.82, -61) * mm});
            skLineSegment(sketch, "E133.left", {"start": v(-540.32, -21.5) * mm, "end": v(-540.32, -58.5) * mm});
            skLineSegment(sketch, "E133.right", {"start": v(-545.32, -21.5) * mm, "end": v(-545.32, -58.5) * mm});
            skPoint(sketch, "E134.visualSharp", {"position": v(-545.32, -19) * mm});
            skArc(sketch, "E134.filletArc", {"start": v(-542.82, -19) * mm, "mid": v(-544.58, -19.73) * mm, "end": v(-545.32, -21.5) * mm});
            skPoint(sketch, "E135.visualSharp", {"position": v(-540.32, -19) * mm});
            skArc(sketch, "E135.filletArc", {"start": v(-540.32, -21.5) * mm, "mid": v(-541.05, -19.73) * mm, "end": v(-542.82, -19) * mm});
            skPoint(sketch, "E136.visualSharp", {"position": v(-545.32, -61) * mm});
            skArc(sketch, "E136.filletArc", {"start": v(-545.32, -58.5) * mm, "mid": v(-544.58, -60.27) * mm, "end": v(-542.82, -61) * mm});
            skPoint(sketch, "E137.visualSharp", {"position": v(-540.32, -61) * mm});
            skArc(sketch, "E137.filletArc", {"start": v(-542.82, -61) * mm, "mid": v(-541.05, -60.27) * mm, "end": v(-540.32, -58.5) * mm});
            skLineSegment(sketch, "E138.bottom", {"start": v(-387.82, -19) * mm, "end": v(-387.82, -19) * mm});
            skLineSegment(sketch, "E138.top", {"start": v(-387.82, -61) * mm, "end": v(-387.82, -61) * mm});
            skLineSegment(sketch, "E138.left", {"start": v(-390.32, -21.5) * mm, "end": v(-390.32, -58.5) * mm});
            skLineSegment(sketch, "E138.right", {"start": v(-385.32, -21.5) * mm, "end": v(-385.32, -58.5) * mm});
            skPoint(sketch, "E139.visualSharp", {"position": v(-390.32, -19) * mm});
            skArc(sketch, "E139.filletArc", {"start": v(-387.82, -19) * mm, "mid": v(-389.58, -19.73) * mm, "end": v(-390.32, -21.5) * mm});
            skPoint(sketch, "E140.visualSharp", {"position": v(-385.32, -19) * mm});
            skArc(sketch, "E140.filletArc", {"start": v(-385.32, -21.5) * mm, "mid": v(-386.05, -19.73) * mm, "end": v(-387.82, -19) * mm});
            skPoint(sketch, "E141.visualSharp", {"position": v(-385.32, -61) * mm});
            skArc(sketch, "E141.filletArc", {"start": v(-387.82, -61) * mm, "mid": v(-386.05, -60.27) * mm, "end": v(-385.32, -58.5) * mm});
            skPoint(sketch, "E142.visualSharp", {"position": v(-390.32, -61) * mm});
            skArc(sketch, "E142.filletArc", {"start": v(-390.32, -58.5) * mm, "mid": v(-389.58, -60.27) * mm, "end": v(-387.82, -61) * mm});
            skSolve(sketch);
        }
        {
            var Q0;
            Q0 = qSketchRegion(id + "F41", true);
            extrude(context, id + "F42", {"entities" : qUnion([Q0]), "depth" : 1 * mm});
        }
        {
            var Q0;
            Q0=qCreatedBy(makeId("Top.planeOp"),FACE);
            var sketch = newSketch(context, id + "F43", { "sketchPlane" : qUnion([Q0])});
            skPoint(sketch, "E143.visualSharp", {"position": v(-384.04, -121.12) * mm});
            skPoint(sketch, "E144.visualSharp", {"position": v(-354.04, -121.12) * mm});
            skLineSegment(sketch, "E145.left", {"start": v(-540.32, 0) * mm, "end": v(-540.32, 0) * mm});
            skLineSegment(sketch, "E145.right", {"start": v(-464.04, -81.12) * mm, "end": v(-464.04, -81.12) * mm});
            skLineSegment(sketch, "E146.right", {"start": v(-384.04, -81.12) * mm, "end": v(-384.04, -81.12) * mm});
            skLineSegment(sketch, "E147.left", {"start": v(-420.32, -81.12) * mm, "end": v(-420.32, -81.12) * mm});
            skPoint(sketch, "E148.visualSharp", {"position": v(-540.32, -5) * mm});
            skLineSegment(sketch, "E149.bottom", {"start": v(-420.32, -81.12) * mm, "end": v(-450.32, -81.12) * mm});
            skLineSegment(sketch, "E149.top", {"start": v(-435.32, -101.12) * mm, "end": v(-435.32, -101.12) * mm});
            skLineSegment(sketch, "E149.left", {"start": v(-420.32, -81.12) * mm, "end": v(-420.32, -86.12) * mm});
            skLineSegment(sketch, "E149.right", {"start": v(-450.32, -81.12) * mm, "end": v(-450.32, -86.12) * mm});
            skPoint(sketch, "E150.visualSharp", {"position": v(-450.32, -101.12) * mm});
            skArc(sketch, "E150.filletArc", {"start": v(-450.32, -86.12) * mm, "mid": v(-445.92, -96.73) * mm, "end": v(-435.32, -101.12) * mm});
            skPoint(sketch, "E151.visualSharp", {"position": v(-420.32, -101.12) * mm});
            skArc(sketch, "E151.filletArc", {"start": v(-435.32, -101.12) * mm, "mid": v(-424.7, -96.73) * mm, "end": v(-420.32, -86.12) * mm});
            skSolve(sketch);
        }
        {
            var Q0;
            Q0 = qSketchRegion(id + "F43", true);
            extrude(context, id + "F44", {"entities" : qUnion([Q0]), "depth" : 1 * mm});
        }
        {
            var Q0;
            Q0=qCreatedBy(makeId("Top.planeOp"),FACE);
            var sketch = newSketch(context, id + "F45", { "sketchPlane" : qUnion([Q0])});
            skLineSegment(sketch, "E152.bottom", {"start": v(-510.32, -81.12) * mm, "end": v(-480.32, -81.12) * mm});
            skLineSegment(sketch, "E152.top", {"start": v(-495.32, -101.12) * mm, "end": v(-495.32, -101.12) * mm});
            skLineSegment(sketch, "E152.left", {"start": v(-510.32, -81.12) * mm, "end": v(-510.32, -86.12) * mm});
            skLineSegment(sketch, "E152.right", {"start": v(-480.32, -81.12) * mm, "end": v(-480.32, -86.12) * mm});
            skPoint(sketch, "E153.visualSharp", {"position": v(-510.32, -101.12) * mm});
            skArc(sketch, "E153.filletArc", {"start": v(-510.32, -86.12) * mm, "mid": v(-505.92, -96.73) * mm, "end": v(-495.32, -101.12) * mm});
            skPoint(sketch, "E154.visualSharp", {"position": v(-480.32, -101.12) * mm});
            skArc(sketch, "E154.filletArc", {"start": v(-495.32, -101.12) * mm, "mid": v(-484.7, -96.73) * mm, "end": v(-480.32, -86.12) * mm});
            skSolve(sketch);
        }
        {
            var Q0;
            Q0 = qSketchRegion(id + "F45", true);
            extrude(context, id + "F46", {"entities" : qUnion([Q0]), "depth" : 1 * mm});
        }
        {
            var Q0;
            Q0=makeQuery(id+"F7.opExtrude","CAP_FACE",FACE,{"disambiguationData":[OSD([sQuery(id+"F6.wireOp",EDGE,"E21"),sQuery(id+"F6.wireOp",EDGE,"E23"),sQuery(id+"F6.wireOp",EDGE,"E24"),sQuery(id+"F6.wireOp",EDGE,"E26.right"),sQuery(id+"F6.wireOp",EDGE,"E27"),sQuery(id+"F6.wireOp",EDGE,"E29.filletArc"),sQuery(id+"F6.wireOp",EDGE,"E30.filletArc"),sQuery(id+"F6.wireOp",EDGE,"E31.filletArc"),sQuery(id+"F6.wireOp",EDGE,"E32.filletArc")])],"isStart":false});
            var sketch = newSketch(context, id + "F47", { "sketchPlane" : qUnion([Q0])});
            skLineSegment(sketch, "E155.bottom", {"start": v(197.85, 42.37) * mm, "end": v(199.85, 42.37) * mm});
            skLineSegment(sketch, "E155.top", {"start": v(197.85, 10.37) * mm, "end": v(199.85, 10.37) * mm});
            skLineSegment(sketch, "E155.left", {"start": v(197.85, 42.37) * mm, "end": v(197.85, 10.37) * mm});
            skLineSegment(sketch, "E155.right", {"start": v(199.85, 42.37) * mm, "end": v(199.85, 10.37) * mm});
            skLineSegment(sketch, "E156", {"start": v(180.6, -11.74) * mm, "end": v(146.08, -31.95) * mm});
            skLineSegment(sketch, "E157", {"start": v(146.08, -31.95) * mm, "end": v(147.09, -33.68) * mm});
            skLineSegment(sketch, "E158", {"start": v(147.09, -33.68) * mm, "end": v(181.6, -13.46) * mm});
            skLineSegment(sketch, "E159", {"start": v(181.6, -13.46) * mm, "end": v(180.6, -11.74) * mm});
            skSolve(sketch);
        }
        {
            var Q0;
            Q0 = qSketchRegion(id + "F47", true);
            extrude(context, id + "F48", {"entities" : qUnion([Q0]), "operationType" : NewBodyOperationType.REMOVE, "oppositeDirection" : true, "depth" : 1 * mm});
        }
        {
            var Q0;
            Q0=makeQuery(id+"F42.opExtrude","SWEPT_BODY",BODY,{"disambiguationData":[OSD([sQuery(id+"F41.wireOp",EDGE,"E130")])]});
            deleteBodies(context, id + "F49", {"entities" : qUnion([Q0])});
        }
        {
            var Q0;
            Q0=makeQuery(id+"F1.opExtrude","CAP_FACE",FACE,{"disambiguationData":[OSD([sQuery(id+"F0.wireOp",EDGE,"E0.bottom"),sQuery(id+"F0.wireOp",EDGE,"E0.top"),sQuery(id+"F0.wireOp",EDGE,"E0.left"),sQuery(id+"F0.wireOp",EDGE,"E0.right")])],"isStart":false});
            var sketch = newSketch(context, id + "F50", { "sketchPlane" : qUnion([Q0])});
            skText(sketch, "E160", { "text": "This\nSide\nUp", "fontName": "OpenSans-Regular.ttf"});
            const initialGuessF50  = {"E160": [-0.05042, 0.0278, 1, 0, 0.01448]};
            skSetInitialGuess(sketch, initialGuessF50);
            skSolve(sketch);
        }
        {
            var Q0;
            Q0 = qSketchRegion(id + "F50", true);
            extrude(context, id + "F51", {"entities" : qUnion([Q0]), "operationType" : NewBodyOperationType.ADD, "depth" : 0.1 * mm});
        }
    });
